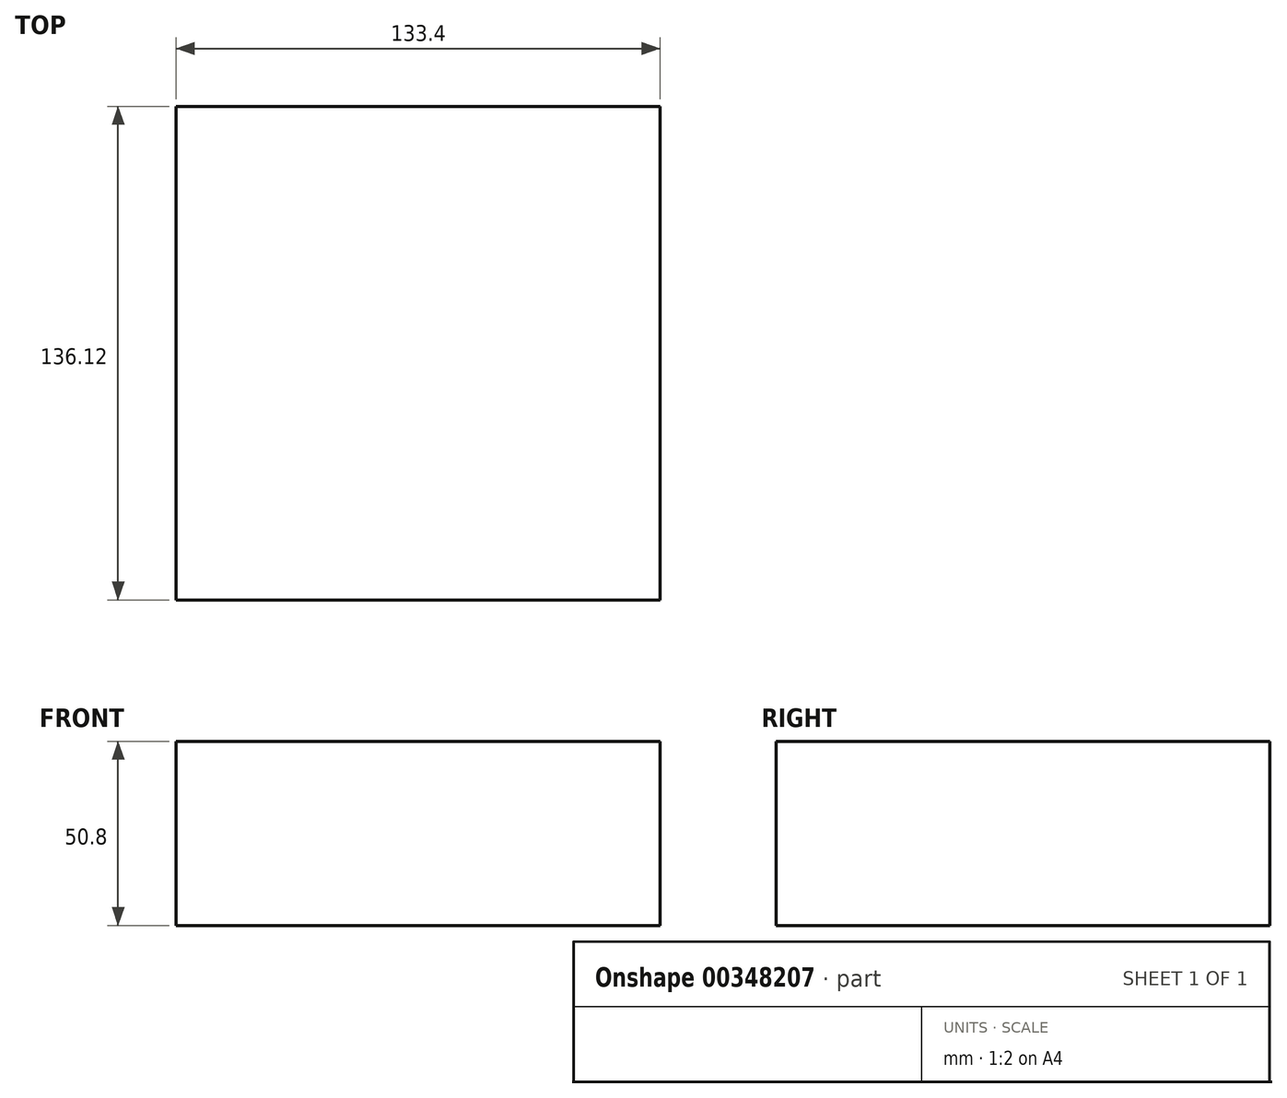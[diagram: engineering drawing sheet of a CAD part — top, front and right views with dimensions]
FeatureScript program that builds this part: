
annotation { "Feature Type Name" : "Feature", "Feature Type Description" : "" }
export const myFeature = defineFeature(function(context is Context, id is Id, definition is map)
    precondition{}
    {
        {
            var Q0;
            Q0=qCreatedBy(makeId("Top.planeOp"),FACE);
            var sketch = newSketch(context, id + "F0", { "sketchPlane" : qUnion([Q0])});
            skLineSegment(sketch, "E0.bottom", {"start": v(66.7, -68.06) * mm, "end": v(-66.7, -68.06) * mm});
            skLineSegment(sketch, "E0.top", {"start": v(66.7, 68.06) * mm, "end": v(-66.7, 68.06) * mm});
            skLineSegment(sketch, "E0.left", {"start": v(66.7, -68.06) * mm, "end": v(66.7, 68.06) * mm});
            skLineSegment(sketch, "E0.right", {"start": v(-66.7, -68.06) * mm, "end": v(-66.7, 68.06) * mm});
            skPoint(sketch, "E0.middle", {"position": v(0, 0) * mm});
            skSolve(sketch);
        }
        {
            var Q0;
            Q0=makeQuery(id+"F0.imprint","IMPRINT",FACE,{"disambiguationData":[TD([[makeQuery(id+"F0.imprint","IMPRINT",EDGE,{"derivedFrom":sQuery(id+"F0.wireOp",EDGE,"E0.bottom")}),-1.0]])]});
            extrude(context, id + "F1", {"entities" : qUnion([Q0]), "depth" : 50.8 * mm});
        }
    });
